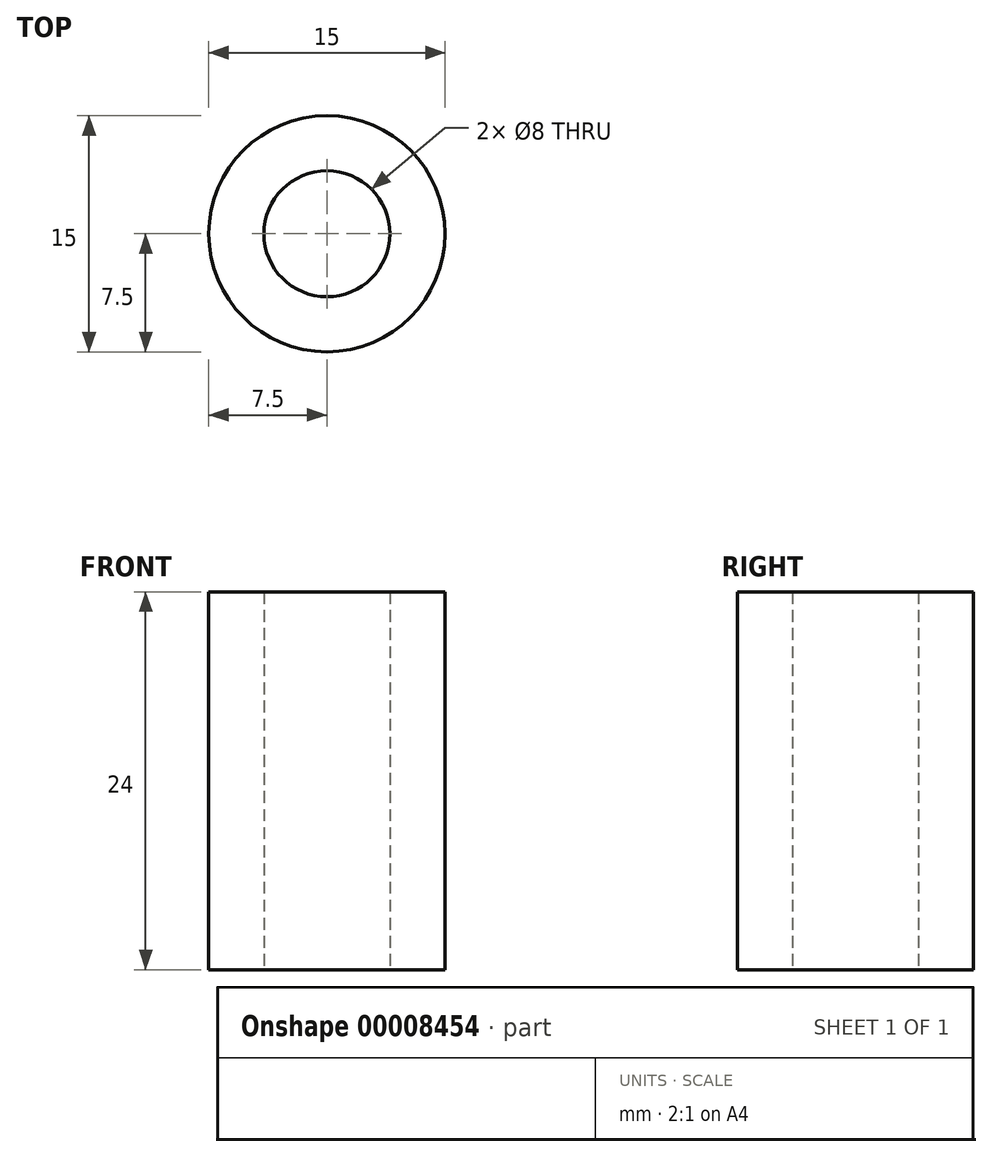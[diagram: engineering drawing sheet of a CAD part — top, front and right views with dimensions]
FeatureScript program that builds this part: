
annotation { "Feature Type Name" : "Feature", "Feature Type Description" : "" }
export const myFeature = defineFeature(function(context is Context, id is Id, definition is map)
    precondition{}
    {
        {
            var Q0;
            Q0=qCreatedBy(makeId("Top.planeOp"),FACE);
            var sketch = newSketch(context, id + "F0", { "sketchPlane" : qUnion([Q0])});
            skCircle(sketch, "E0", {"center": v(0, 0) * mm, "radius": 4 * mm});
            skCircle(sketch, "E1", {"center": v(0, 0) * mm, "radius": 7.5 * mm});
            skSolve(sketch);
        }
        {
            var Q0;
            Q0=makeQuery(id+"F0.imprint","IMPRINT",FACE,{"disambiguationData":[TD([[makeQuery(id+"F0.imprint","IMPRINT",EDGE,{"derivedFrom":sQuery(id+"F0.wireOp",EDGE,"E0")}),-1.0]])]});
            extrude(context, id + "F1", {"entities" : qUnion([Q0]), "depth" : 24 * mm});
        }
    });
